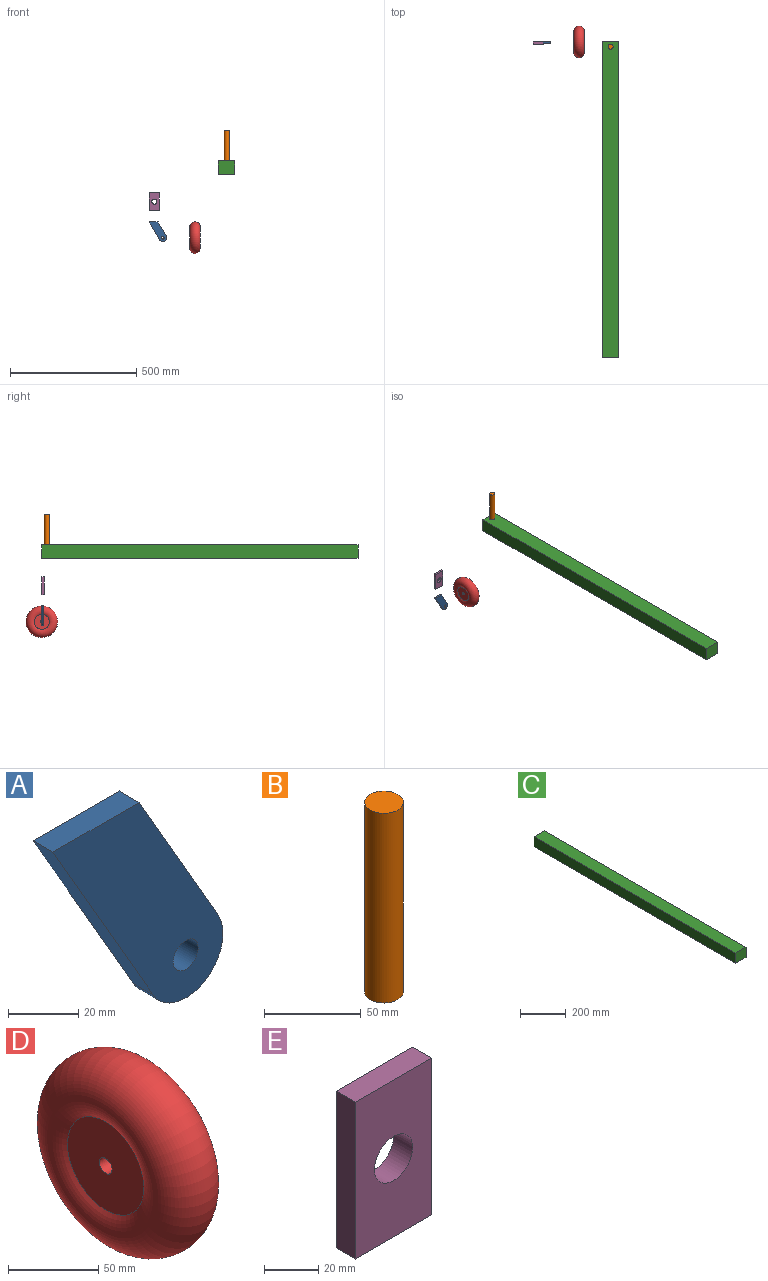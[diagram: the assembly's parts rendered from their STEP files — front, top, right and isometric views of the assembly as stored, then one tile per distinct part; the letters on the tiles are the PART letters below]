
ASSEMBLY  parts=5 mates=1
PART A: 7 faces, bbox 68.4x8x77.5 mm
  f0: plane 34.64x8mm, normal (0,0,1), area 277.1mm2, adj f1,f4,f5,f6
  f1: plane 70x40.41mm, normal (-0.87,0,-0.5), area 646.6mm2, adj f0,f2,f5,f6
  f2: cylinder r=15mm len=27.99mm, axis (0,1,0), area 377mm2, adj f1,f4,f5,f6
  f3: cylinder r=5mm len=10mm, axis (0,1,0), area 251.3mm2, adj f5,f6
  f4: plane 55x31.75mm, normal (0.87,0,0.5), area 508.1mm2, adj f0,f2,f5,f6
  f5: plane 77.5x68.41mm, normal (0,-1,0), area 2440mm2, adj f0,f1,f2,f3,f4
  f6: plane 77.5x68.41mm, normal (0,1,0), area 2440mm2, adj f0,f1,f2,f3,f4
PART B: 3 faces, bbox 20x20x120 mm
  f0: plane 20x20mm, normal (0,0,1), area 314.2mm2, adj f1
  f1: cylinder r=10mm len=120mm, axis (0,0,1), area 7539.8mm2, adj f0,f2
  f2: plane 20x20mm, normal (0,0,-1), area 314.2mm2, adj f1
PART C: 6 faces, bbox 64.2x1250x53.9 mm
  f0: plane 1250x64.23mm, normal (0,0,1), area 80283.5mm2, adj f1,f3,f4,f5
  f1: plane 1250x53.89mm, normal (-1,0,0), area 67363.8mm2, adj f0,f2,f4,f5
  f2: plane 1250x64.23mm, normal (0,0,-1), area 80283.5mm2, adj f1,f3,f4,f5
  f3: plane 1250x53.89mm, normal (1,0,0), area 67363.8mm2, adj f0,f2,f4,f5
  f4: plane 64.23x53.89mm, normal (0,-1,0), area 3461.2mm2, adj f0,f1,f2,f3
  f5: plane 64.23x53.89mm, normal (0,1,0), area 3461.2mm2, adj f0,f1,f2,f3
PART D: 4 faces, bbox 41.9x135.3x135.3 mm
  f0: cylinder r=5mm len=35mm, axis (-1,0,0), area 1099.6mm2, adj f1,f3
  f1: plane 60x60mm, normal (1,0,0), area 2748.9mm2, adj f0,f2
  f2: torus R=41.54mm, axis (-1,0,0), area 28174.9mm2, adj f1,f3
  f3: plane 60x60mm, normal (-1,0,0), area 2748.9mm2, adj f0,f2
PART E: 7 faces, bbox 40x10x71 mm
  f0: plane 71x10mm, normal (-1,0,0), area 710mm2, adj f1,f3,f5,f6
  f1: plane 40x10mm, normal (0,0,-1), area 400mm2, adj f0,f2,f5,f6
  f2: plane 71x10mm, normal (1,0,0), area 710mm2, adj f1,f3,f5,f6
  f3: plane 40x10mm, normal (0,0,1), area 400mm2, adj f0,f2,f5,f6
  f4: cylinder r=10mm len=20mm, axis (0,1,0), area 628.3mm2, adj f5,f6
  f5: plane 71x40mm, normal (0,-1,0), area 2525.8mm2, adj f0,f1,f2,f3,f4
  f6: plane 71x40mm, normal (0,1,0), area 2525.8mm2, adj f0,f1,f2,f3,f4
PLACE A t=(-620.97,158.22,-237.42)mm
PLACE B rot(axis=(1,0,0),180deg) t=(-335.42,138.22,317.76)mm
PLACE C t=(-620.97,158.22,-237.42)mm
PLACE D t=(-620.97,158.22,-237.42)mm
PLACE E t=(-620.97,158.22,-237.42)mm
MATE fastened B.f1 <-> C.f0  axis (0,0,-1) through (-452.36,138.22,20.41)mm
